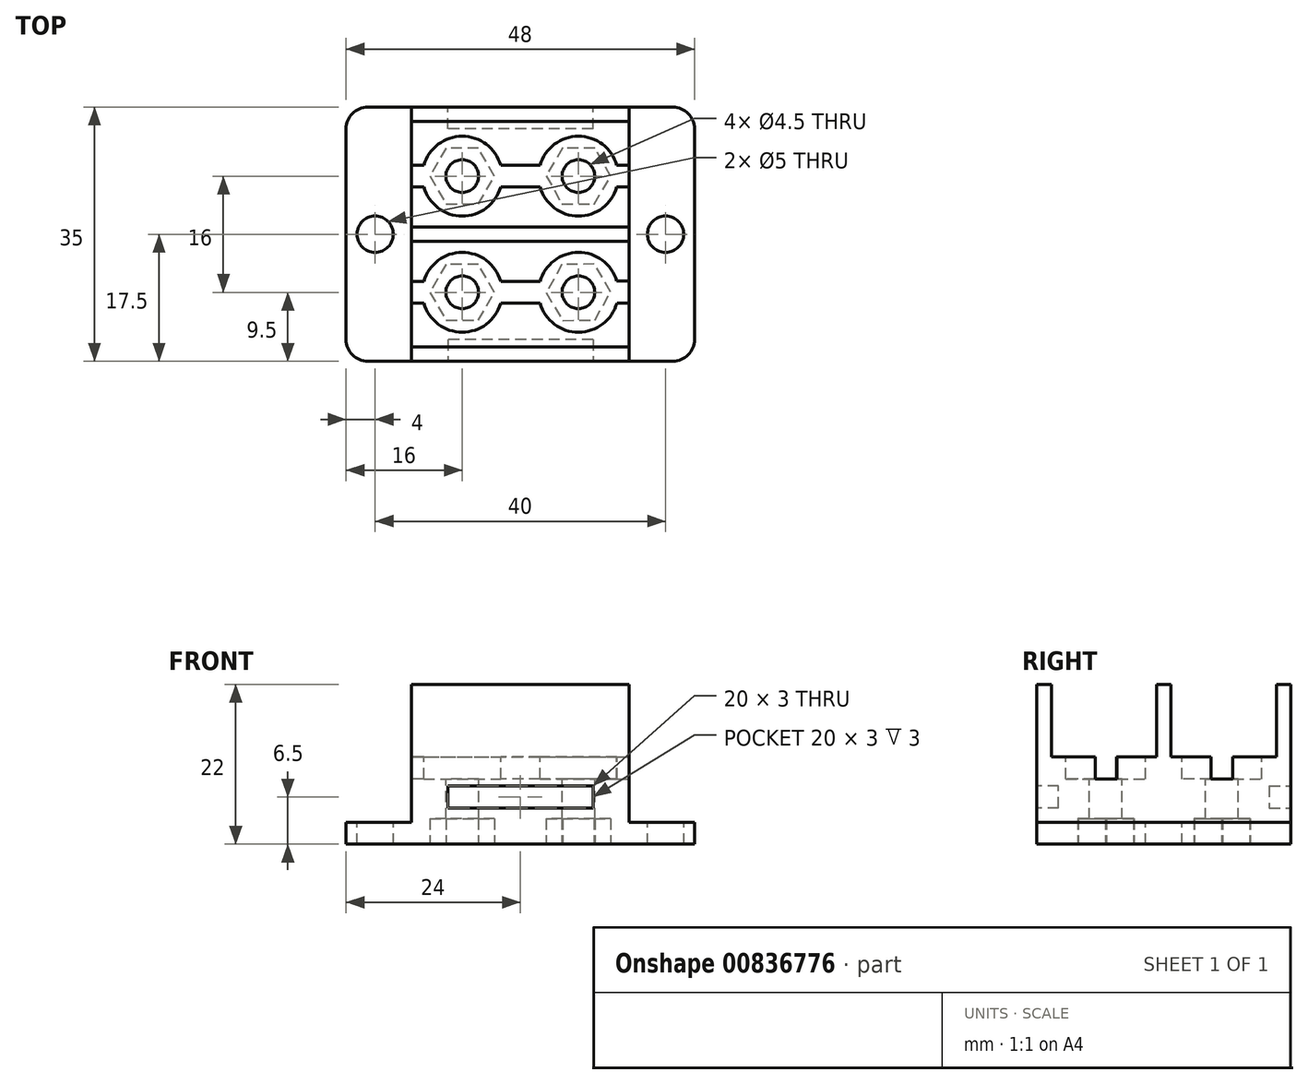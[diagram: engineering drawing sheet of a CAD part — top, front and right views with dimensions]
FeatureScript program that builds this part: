
annotation { "Feature Type Name" : "Feature", "Feature Type Description" : "" }
export const myFeature = defineFeature(function(context is Context, id is Id, definition is map)
    precondition{}
    {
        {
            var Q0;
            Q0=qCreatedBy(makeId("Front.planeOp"),FACE);
            var sketch = newSketch(context, id + "F0", { "sketchPlane" : qUnion([Q0])});
            skLineSegment(sketch, "E0", {"start": v(0, 0) * mm, "end": v(-9, 0) * mm});
            skLineSegment(sketch, "E1", {"start": v(-9, 0) * mm, "end": v(-9, 3) * mm});
            skLineSegment(sketch, "E2", {"start": v(-9, 3) * mm, "end": v(0, 3) * mm});
            skLineSegment(sketch, "E3", {"start": v(0, 3) * mm, "end": v(0, 12) * mm});
            skLineSegment(sketch, "E4", {"start": v(0, 12) * mm, "end": v(30, 12) * mm});
            skLineSegment(sketch, "E5", {"start": v(30, 12) * mm, "end": v(30, 3) * mm});
            skLineSegment(sketch, "E6", {"start": v(30, 3) * mm, "end": v(39, 3) * mm});
            skLineSegment(sketch, "E7", {"start": v(39, 3) * mm, "end": v(39, 0) * mm});
            skLineSegment(sketch, "E8", {"start": v(39, 0) * mm, "end": v(0, 0) * mm});
            skSolve(sketch);
        }
        {
            var Q0;
            Q0=makeQuery(id+"F0.imprint","IMPRINT",FACE,{"disambiguationData":[TD([[makeQuery(id+"F0.imprint","IMPRINT",EDGE,{"derivedFrom":sQuery(id+"F0.wireOp",EDGE,"E0")}),-1.0]])]});
            extrude(context, id + "F1", {"entities" : qUnion([Q0]), "oppositeDirection" : true, "depth" : 35 * mm, "offsetDistance" : 25 * mm});
        }
        {
            var Q0;
            Q0=qCreatedBy(makeId("Top.planeOp"),FACE);
            var Q1;
            Q1=makeQuery(id+"F1.opExtrude","CAP_VERTEX",VERTEX,{"disambiguationData":[OSD([sQuery(id+"F0.wireOp",EDGE,"E3"),sQuery(id+"F0.wireOp",EDGE,"E4")])],"isStart":false});
            cPlane(context, id + "F2", {"entities" : qUnion([Q0, Q1]), "cplaneType" : CPlaneType.PLANE_POINT, "offset" : 25 * mm, "width" : 150 * mm, "height" : 150 * mm});
        }
        {
            var Q0;
            Q0=qCreatedBy(id+"F2.planeOp",FACE);
            var sketch = newSketch(context, id + "F3", { "sketchPlane" : qUnion([Q0])});
            skLineSegment(sketch, "E9", {"start": v(23, 53.6) * mm, "end": v(23, -24.59) * mm, "construction": true});
            skLineSegment(sketch, "E10", {"start": v(7, 50.62) * mm, "end": v(7, -28.29) * mm, "construction": true});
            skLineSegment(sketch, "E11", {"start": v(23.6, 25.5) * mm, "end": v(1.01, 25.5) * mm, "construction": true});
            skLineSegment(sketch, "E12", {"start": v(28.02, 9.5) * mm, "end": v(4.88, 9.5) * mm, "construction": true});
            skCircle(sketch, "E13", {"center": v(23, 25.5) * mm, "radius": 2.25 * mm});
            skCircle(sketch, "E14", {"center": v(23, 9.5) * mm, "radius": 2.25 * mm});
            skCircle(sketch, "E15", {"center": v(7, 25.5) * mm, "radius": 2.25 * mm});
            skCircle(sketch, "E16", {"center": v(7, 9.5) * mm, "radius": 2.25 * mm});
            skLineSegment(sketch, "E17.bottom", {"start": v(29.45, 0) * mm, "end": v(0, 0) * mm});
            skLineSegment(sketch, "E18.bottom", {"start": v(8.68, 27) * mm, "end": v(21.32, 27) * mm});
            skLineSegment(sketch, "E18.top", {"start": v(8.68, 24) * mm, "end": v(21.32, 24) * mm});
            skLineSegment(sketch, "E18.left", {"start": v(8.68, 27) * mm, "end": v(8.68, 24) * mm});
            skLineSegment(sketch, "E18.right", {"start": v(21.32, 27) * mm, "end": v(21.32, 24) * mm});
            skLineSegment(sketch, "E19", {"start": v(8.68, 11) * mm, "end": v(21.32, 11) * mm});
            skLineSegment(sketch, "E20", {"start": v(21.32, 11) * mm, "end": v(21.32, 8) * mm});
            skLineSegment(sketch, "E21", {"start": v(21.32, 8) * mm, "end": v(8.68, 8) * mm});
            skLineSegment(sketch, "E22", {"start": v(8.68, 8) * mm, "end": v(8.68, 11) * mm});
            skCircle(sketch, "E23", {"center": v(7, 25.5) * mm, "radius": 5.5 * mm});
            skCircle(sketch, "E24", {"center": v(23, 25.5) * mm, "radius": 5.5 * mm});
            skCircle(sketch, "E25", {"center": v(7, 9.5) * mm, "radius": 5.5 * mm});
            skCircle(sketch, "E26", {"center": v(23, 9.5) * mm, "radius": 5.5 * mm});
            skLineSegment(sketch, "E27.bottom", {"start": v(28.3, 27) * mm, "end": v(30.07, 27) * mm});
            skLineSegment(sketch, "E28.bottom", {"start": v(5.32, 27) * mm, "end": v(0, 27) * mm});
            skLineSegment(sketch, "E28.top", {"start": v(5.32, 24) * mm, "end": v(0, 24) * mm});
            skLineSegment(sketch, "E28.left", {"start": v(5.32, 27) * mm, "end": v(5.32, 24) * mm});
            skLineSegment(sketch, "E28.right", {"start": v(0, 27) * mm, "end": v(0, 24) * mm});
            skLineSegment(sketch, "E29.bottom", {"start": v(24.68, 27) * mm, "end": v(30, 27) * mm});
            skLineSegment(sketch, "E29.top", {"start": v(24.68, 24) * mm, "end": v(30, 24) * mm});
            skLineSegment(sketch, "E29.left", {"start": v(24.68, 27) * mm, "end": v(24.68, 24) * mm});
            skLineSegment(sketch, "E29.right", {"start": v(30, 27) * mm, "end": v(30, 24) * mm});
            skLineSegment(sketch, "E30.bottom", {"start": v(5.32, 11) * mm, "end": v(0, 11) * mm});
            skLineSegment(sketch, "E30.top", {"start": v(5.32, 8) * mm, "end": v(0, 8) * mm});
            skLineSegment(sketch, "E30.left", {"start": v(5.32, 11) * mm, "end": v(5.32, 8) * mm});
            skLineSegment(sketch, "E30.right", {"start": v(0, 11) * mm, "end": v(0, 8) * mm});
            skLineSegment(sketch, "E31.bottom", {"start": v(24.64, 11.04) * mm, "end": v(30, 11.04) * mm});
            skLineSegment(sketch, "E31.top", {"start": v(24.64, 8.04) * mm, "end": v(30, 8.04) * mm});
            skLineSegment(sketch, "E31.left", {"start": v(24.64, 11.04) * mm, "end": v(24.64, 8.04) * mm});
            skLineSegment(sketch, "E31.right", {"start": v(30, 11.04) * mm, "end": v(30, 8.04) * mm});
            skSolve(sketch);
        }
        {
            var Q0;
            Q0=makeQuery(id+"F1.opExtrude","SWEPT_FACE",FACE,{"disambiguationData":[OSD([sQuery(id+"F0.wireOp",EDGE,"E6")])]});
            var sketch = newSketch(context, id + "F4", { "sketchPlane" : qUnion([Q0])});
            skCircle(sketch, "E32", {"center": v(-5, 17.5) * mm, "radius": 2.5 * mm});
            skCircle(sketch, "E33", {"center": v(35, 17.5) * mm, "radius": 2.5 * mm});
            skSolve(sketch);
        }
        {
            var Q0;
            Q0=makeQuery(id+"F4.imprint","IMPRINT",FACE,{"disambiguationData":[TD([[makeQuery(id+"F4.imprint","IMPRINT",EDGE,{"derivedFrom":sQuery(id+"F4.wireOp",EDGE,"E32")}),1.0]])]});
            var Q1;
            Q1=makeQuery(id+"F4.imprint","IMPRINT",FACE,{"disambiguationData":[TD([[makeQuery(id+"F4.imprint","IMPRINT",EDGE,{"derivedFrom":sQuery(id+"F4.wireOp",EDGE,"E33")}),1.0]])]});
            extrude(context, id + "F5", {"entities" : qUnion([Q0, Q1]), "operationType" : NewBodyOperationType.REMOVE, "endBound" : BoundingType.UP_TO_NEXT, "oppositeDirection" : true, "depth" : 25 * mm, "offsetDistance" : 25 * mm});
        }
        {
            var Q0;
            Q0=makeQuery(id+"F1.opExtrude","CAP_EDGE",EDGE,{"disambiguationData":[OSD([sQuery(id+"F0.wireOp",EDGE,"E1")])],"isStart":false});
            var Q1;
            Q1=makeQuery(id+"F1.opExtrude","CAP_EDGE",EDGE,{"disambiguationData":[OSD([sQuery(id+"F0.wireOp",EDGE,"E7")])],"isStart":false});
            var Q2;
            Q2=makeQuery(id+"F1.opExtrude","CAP_EDGE",EDGE,{"disambiguationData":[OSD([sQuery(id+"F0.wireOp",EDGE,"E7")])],"isStart":true});
            var Q3;
            Q3=makeQuery(id+"F1.opExtrude","CAP_EDGE",EDGE,{"disambiguationData":[OSD([sQuery(id+"F0.wireOp",EDGE,"E1")])],"isStart":true});
            fillet(context, id + "F6", {"entities" : qUnion([Q0, Q1, Q2, Q3]), "radius" : 3 * mm, "tangentPropagation" : true, "allowEdgeOverflow" : false});
        }
        {
            var Q0;
            Q0=makeQuery(id+"F1.opExtrude","SWEPT_FACE",FACE,{"disambiguationData":[OSD([sQuery(id+"F0.wireOp",EDGE,"E4")])]});
            var sketch = newSketch(context, id + "F7", { "sketchPlane" : qUnion([Q0])});
            skLineSegment(sketch, "E34.bottom", {"start": v(0, 35) * mm, "end": v(30, 35) * mm});
            skLineSegment(sketch, "E34.top", {"start": v(0, 33) * mm, "end": v(30, 33) * mm});
            skLineSegment(sketch, "E34.left", {"start": v(0, 35) * mm, "end": v(0, 33) * mm});
            skLineSegment(sketch, "E34.right", {"start": v(30, 35) * mm, "end": v(30, 33) * mm});
            skLineSegment(sketch, "E35.bottom", {"start": v(0, 18.5) * mm, "end": v(30, 18.5) * mm});
            skLineSegment(sketch, "E35.top", {"start": v(0, 16.5) * mm, "end": v(30, 16.5) * mm});
            skLineSegment(sketch, "E35.left", {"start": v(0, 18.5) * mm, "end": v(0, 16.5) * mm});
            skLineSegment(sketch, "E35.right", {"start": v(30, 18.5) * mm, "end": v(30, 16.5) * mm});
            skLineSegment(sketch, "E36.bottom", {"start": v(0, 0) * mm, "end": v(30, 0) * mm});
            skLineSegment(sketch, "E36.top", {"start": v(0, 2) * mm, "end": v(30, 2) * mm});
            skLineSegment(sketch, "E36.left", {"start": v(0, 0) * mm, "end": v(0, 2) * mm});
            skLineSegment(sketch, "E36.right", {"start": v(30, 0) * mm, "end": v(30, 2) * mm});
            skSolve(sketch);
        }
        {
            var Q0;
            Q0=makeQuery(id+"F7.imprint","IMPRINT",FACE,{"disambiguationData":[TD([[makeQuery(id+"F7.imprint","IMPRINT",EDGE,{"derivedFrom":sQuery(id+"F7.wireOp",EDGE,"E34.bottom")}),-1.0]])]});
            var Q1;
            Q1=makeQuery(id+"F7.imprint","IMPRINT",FACE,{"disambiguationData":[TD([[makeQuery(id+"F7.imprint","IMPRINT",EDGE,{"derivedFrom":sQuery(id+"F7.wireOp",EDGE,"E35.bottom")}),-1.0]])]});
            var Q2;
            Q2=makeQuery(id+"F7.imprint","IMPRINT",FACE,{"disambiguationData":[TD([[makeQuery(id+"F7.imprint","IMPRINT",EDGE,{"derivedFrom":sQuery(id+"F7.wireOp",EDGE,"E36.bottom")}),1.0]])]});
            extrude(context, id + "F8", {"entities" : qUnion([Q0, Q1, Q2]), "operationType" : NewBodyOperationType.ADD, "depth" : 10 * mm, "offsetDistance" : 25 * mm});
        }
        {
            var Q0;
            {var subQ0=sQuery(id+"F3.wireOp",EDGE,"E18.left");Q0=makeQuery(id+"F3.imprint","IMPRINT",FACE,{"disambiguationData":[TD([[makeQuery(id+"F3.imprint","IMPRINT",EDGE,{"derivedFrom":subQ0}),-1.0]])]});}
            var Q1;
            {var subQ0=sQuery(id+"F3.wireOp",EDGE,"E28.left");Q1=makeQuery(id+"F3.imprint","IMPRINT",FACE,{"disambiguationData":[TD([[makeQuery(id+"F3.imprint","IMPRINT",EDGE,{"derivedFrom":subQ0}),-1.0]])]});}
            var Q2;
            {var subQ0=sQuery(id+"F3.wireOp",EDGE,"E18.left");Q2=makeQuery(id+"F3.imprint","IMPRINT",FACE,{"disambiguationData":[TD([[makeQuery(id+"F3.imprint","IMPRINT",EDGE,{"derivedFrom":subQ0}),1.0]])]});}
            var Q3;
            {var subQ0=sQuery(id+"F3.wireOp",EDGE,"E18.right");Q3=makeQuery(id+"F3.imprint","IMPRINT",FACE,{"disambiguationData":[TD([[makeQuery(id+"F3.imprint","IMPRINT",EDGE,{"derivedFrom":subQ0}),-1.0]])]});}
            var Q4;
            {var subQ0=sQuery(id+"F3.wireOp",EDGE,"E29.left");Q4=makeQuery(id+"F3.imprint","IMPRINT",FACE,{"disambiguationData":[TD([[makeQuery(id+"F3.imprint","IMPRINT",EDGE,{"derivedFrom":subQ0}),1.0]])]});}
            var Q5;
            {var subQ0=sQuery(id+"F3.wireOp",EDGE,"E18.right");Q5=makeQuery(id+"F3.imprint","IMPRINT",FACE,{"disambiguationData":[TD([[makeQuery(id+"F3.imprint","IMPRINT",EDGE,{"derivedFrom":subQ0}),1.0]])]});}
            var Q6;
            {var subQ0=sQuery(id+"F3.wireOp",EDGE,"E22");Q6=makeQuery(id+"F3.imprint","IMPRINT",FACE,{"disambiguationData":[TD([[makeQuery(id+"F3.imprint","IMPRINT",EDGE,{"derivedFrom":subQ0}),1.0]])]});}
            var Q7;
            {var subQ0=sQuery(id+"F3.wireOp",EDGE,"E22");Q7=makeQuery(id+"F3.imprint","IMPRINT",FACE,{"disambiguationData":[TD([[makeQuery(id+"F3.imprint","IMPRINT",EDGE,{"derivedFrom":subQ0}),-1.0]])]});}
            var Q8;
            {var subQ0=sQuery(id+"F3.wireOp",EDGE,"E30.left");Q8=makeQuery(id+"F3.imprint","IMPRINT",FACE,{"disambiguationData":[TD([[makeQuery(id+"F3.imprint","IMPRINT",EDGE,{"derivedFrom":subQ0}),-1.0]])]});}
            var Q9;
            {var subQ0=sQuery(id+"F3.wireOp",EDGE,"E20");Q9=makeQuery(id+"F3.imprint","IMPRINT",FACE,{"disambiguationData":[TD([[makeQuery(id+"F3.imprint","IMPRINT",EDGE,{"derivedFrom":subQ0}),-1.0]])]});}
            var Q10;
            {var subQ0=sQuery(id+"F3.wireOp",EDGE,"E31.left");Q10=makeQuery(id+"F3.imprint","IMPRINT",FACE,{"disambiguationData":[TD([[makeQuery(id+"F3.imprint","IMPRINT",EDGE,{"derivedFrom":subQ0}),1.0]])]});}
            var Q11;
            {var subQ4=sQuery(id+"F3.wireOp",EDGE,"E20");Q11=makeQuery(id+"F3.imprint","IMPRINT",FACE,{"disambiguationData":[TD([[makeQuery(id+"F3.imprint","IMPRINT",EDGE,{"derivedFrom":subQ4}),1.0]])]});}
            extrude(context, id + "F9", {"entities" : qUnion([Q0, Q1, Q2, Q3, Q4, Q5, Q6, Q7, Q8, Q9, Q10, Q11]), "operationType" : NewBodyOperationType.REMOVE, "endBound" : BoundingType.UP_TO_NEXT, "oppositeDirection" : true, "depth" : 25 * mm, "offsetDistance" : 25 * mm});
        }
        {
            var Q0;
            {var subQ0=sQuery(id+"F3.wireOp",EDGE,"E21");var subQ5=sQuery(id+"F3.wireOp",EDGE,"E25");var subQ6=makeQuery(id+"F3.imprint","INTERSECT",VERTEX,{"derivedFrom":[subQ0,subQ5]});Q0=makeQuery(id+"F3.imprint","IMPRINT",FACE,{"disambiguationData":[TD([[makeQuery(id+"F3.imprint","IMPRINT",EDGE,{"disambiguationData":[TD([[subQ6,1.0]])],"derivedFrom":subQ5}),1.0]])]});}
            var Q1;
            {var subQ1=sQuery(id+"F3.wireOp",EDGE,"E30.bottom");var subQ6=sQuery(id+"F3.wireOp",EDGE,"E25");var subQ7=makeQuery(id+"F3.imprint","INTERSECT",VERTEX,{"derivedFrom":[subQ6,subQ1]});Q1=makeQuery(id+"F3.imprint","IMPRINT",FACE,{"disambiguationData":[TD([[makeQuery(id+"F3.imprint","IMPRINT",EDGE,{"disambiguationData":[TD([[subQ7,-1.0]])],"derivedFrom":subQ6}),1.0]])]});}
            var Q2;
            {var subQ0=sQuery(id+"F3.wireOp",EDGE,"E19");var subQ5=sQuery(id+"F3.wireOp",EDGE,"E25");var subQ6=makeQuery(id+"F3.imprint","INTERSECT",VERTEX,{"derivedFrom":[subQ0,subQ5]});Q2=makeQuery(id+"F3.imprint","IMPRINT",FACE,{"disambiguationData":[TD([[makeQuery(id+"F3.imprint","IMPRINT",EDGE,{"disambiguationData":[TD([[subQ6,-1.0]])],"derivedFrom":subQ5}),1.0]])]});}
            var Q3;
            {var subQ1=sQuery(id+"F3.wireOp",EDGE,"E19");var subQ6=sQuery(id+"F3.wireOp",EDGE,"E25");var subQ8=makeQuery(id+"F3.imprint","INTERSECT",VERTEX,{"derivedFrom":[subQ1,subQ6]});Q3=makeQuery(id+"F3.imprint","IMPRINT",FACE,{"disambiguationData":[TD([[makeQuery(id+"F3.imprint","IMPRINT",EDGE,{"disambiguationData":[TD([[subQ8,1.0]])],"derivedFrom":subQ6}),1.0]])]});}
            var Q4;
            {var subQ0=sQuery(id+"F3.wireOp",EDGE,"E19");var subQ5=sQuery(id+"F3.wireOp",EDGE,"E26");var subQ6=makeQuery(id+"F3.imprint","INTERSECT",VERTEX,{"derivedFrom":[subQ0,subQ5]});Q4=makeQuery(id+"F3.imprint","IMPRINT",FACE,{"disambiguationData":[TD([[makeQuery(id+"F3.imprint","IMPRINT",EDGE,{"disambiguationData":[TD([[subQ6,1.0]])],"derivedFrom":subQ5}),1.0]])]});}
            var Q5;
            {var subQ1=sQuery(id+"F3.wireOp",EDGE,"E19");var subQ6=sQuery(id+"F3.wireOp",EDGE,"E26");var subQ7=makeQuery(id+"F3.imprint","INTERSECT",VERTEX,{"derivedFrom":[subQ1,subQ6]});Q5=makeQuery(id+"F3.imprint","IMPRINT",FACE,{"disambiguationData":[TD([[makeQuery(id+"F3.imprint","IMPRINT",EDGE,{"disambiguationData":[TD([[subQ7,-1.0]])],"derivedFrom":subQ6}),1.0]])]});}
            var Q6;
            {var subQ0=sQuery(id+"F3.wireOp",EDGE,"E21");var subQ5=sQuery(id+"F3.wireOp",EDGE,"E26");var subQ6=makeQuery(id+"F3.imprint","INTERSECT",VERTEX,{"derivedFrom":[subQ0,subQ5]});Q6=makeQuery(id+"F3.imprint","IMPRINT",FACE,{"disambiguationData":[TD([[makeQuery(id+"F3.imprint","IMPRINT",EDGE,{"disambiguationData":[TD([[subQ6,-1.0]])],"derivedFrom":subQ5}),1.0]])]});}
            var Q7;
            {var subQ0=sQuery(id+"F3.wireOp",EDGE,"E31.bottom");var subQ5=sQuery(id+"F3.wireOp",EDGE,"E26");var subQ6=makeQuery(id+"F3.imprint","INTERSECT",VERTEX,{"derivedFrom":[subQ5,subQ0]});Q7=makeQuery(id+"F3.imprint","IMPRINT",FACE,{"disambiguationData":[TD([[makeQuery(id+"F3.imprint","IMPRINT",EDGE,{"disambiguationData":[TD([[subQ6,1.0]])],"derivedFrom":subQ5}),1.0]])]});}
            var Q8;
            {var subQ0=sQuery(id+"F3.wireOp",EDGE,"E18.top");var subQ5=sQuery(id+"F3.wireOp",EDGE,"E24");var subQ6=makeQuery(id+"F3.imprint","INTERSECT",VERTEX,{"derivedFrom":[subQ0,subQ5]});Q8=makeQuery(id+"F3.imprint","IMPRINT",FACE,{"disambiguationData":[TD([[makeQuery(id+"F3.imprint","IMPRINT",EDGE,{"disambiguationData":[TD([[subQ6,-1.0]])],"derivedFrom":subQ5}),1.0]])]});}
            var Q9;
            {var subQ1=sQuery(id+"F3.wireOp",EDGE,"E29.bottom");var subQ6=sQuery(id+"F3.wireOp",EDGE,"E24");var subQ7=makeQuery(id+"F3.imprint","INTERSECT",VERTEX,{"derivedFrom":[subQ6,subQ1]});Q9=makeQuery(id+"F3.imprint","IMPRINT",FACE,{"disambiguationData":[TD([[makeQuery(id+"F3.imprint","IMPRINT",EDGE,{"disambiguationData":[TD([[subQ7,1.0]])],"derivedFrom":subQ6}),1.0]])]});}
            var Q10;
            {var subQ0=sQuery(id+"F3.wireOp",EDGE,"E18.bottom");var subQ5=sQuery(id+"F3.wireOp",EDGE,"E24");var subQ6=makeQuery(id+"F3.imprint","INTERSECT",VERTEX,{"derivedFrom":[subQ0,subQ5]});Q10=makeQuery(id+"F3.imprint","IMPRINT",FACE,{"disambiguationData":[TD([[makeQuery(id+"F3.imprint","IMPRINT",EDGE,{"disambiguationData":[TD([[subQ6,1.0]])],"derivedFrom":subQ5}),1.0]])]});}
            var Q11;
            {var subQ1=sQuery(id+"F3.wireOp",EDGE,"E18.bottom");var subQ6=sQuery(id+"F3.wireOp",EDGE,"E24");var subQ8=makeQuery(id+"F3.imprint","INTERSECT",VERTEX,{"derivedFrom":[subQ1,subQ6]});Q11=makeQuery(id+"F3.imprint","IMPRINT",FACE,{"disambiguationData":[TD([[makeQuery(id+"F3.imprint","IMPRINT",EDGE,{"disambiguationData":[TD([[subQ8,-1.0]])],"derivedFrom":subQ6}),1.0]])]});}
            var Q12;
            {var subQ0=sQuery(id+"F3.wireOp",EDGE,"E18.top");var subQ5=sQuery(id+"F3.wireOp",EDGE,"E23");var subQ7=makeQuery(id+"F3.imprint","INTERSECT",VERTEX,{"derivedFrom":[subQ0,subQ5]});Q12=makeQuery(id+"F3.imprint","IMPRINT",FACE,{"disambiguationData":[TD([[makeQuery(id+"F3.imprint","IMPRINT",EDGE,{"disambiguationData":[TD([[subQ7,1.0]])],"derivedFrom":subQ5}),1.0]])]});}
            var Q13;
            {var subQ0=sQuery(id+"F3.wireOp",EDGE,"E18.bottom");var subQ5=sQuery(id+"F3.wireOp",EDGE,"E23");var subQ7=makeQuery(id+"F3.imprint","INTERSECT",VERTEX,{"derivedFrom":[subQ0,subQ5]});Q13=makeQuery(id+"F3.imprint","IMPRINT",FACE,{"disambiguationData":[TD([[makeQuery(id+"F3.imprint","IMPRINT",EDGE,{"disambiguationData":[TD([[subQ7,-1.0]])],"derivedFrom":subQ5}),1.0]])]});}
            var Q14;
            {var subQ1=sQuery(id+"F3.wireOp",EDGE,"E18.bottom");var subQ6=sQuery(id+"F3.wireOp",EDGE,"E23");var subQ7=makeQuery(id+"F3.imprint","INTERSECT",VERTEX,{"derivedFrom":[subQ1,subQ6]});Q14=makeQuery(id+"F3.imprint","IMPRINT",FACE,{"disambiguationData":[TD([[makeQuery(id+"F3.imprint","IMPRINT",EDGE,{"disambiguationData":[TD([[subQ7,1.0]])],"derivedFrom":subQ6}),1.0]])]});}
            var Q15;
            {var subQ1=sQuery(id+"F3.wireOp",EDGE,"E28.bottom");var subQ6=sQuery(id+"F3.wireOp",EDGE,"E23");var subQ7=makeQuery(id+"F3.imprint","INTERSECT",VERTEX,{"derivedFrom":[subQ6,subQ1]});Q15=makeQuery(id+"F3.imprint","IMPRINT",FACE,{"disambiguationData":[TD([[makeQuery(id+"F3.imprint","IMPRINT",EDGE,{"disambiguationData":[TD([[subQ7,-1.0]])],"derivedFrom":subQ6}),1.0]])]});}
            extrude(context, id + "F10", {"entities" : qUnion([Q0, Q1, Q2, Q3, Q4, Q5, Q6, Q7, Q8, Q9, Q10, Q11, Q12, Q13, Q14, Q15]), "operationType" : NewBodyOperationType.REMOVE, "oppositeDirection" : true, "depth" : 3 * mm, "offsetDistance" : 25 * mm});
        }
        {
            var Q0;
            Q0 = qSketchRegion(id + "F3", true);
            extrude(context, id + "F11", {"entities" : qUnion([Q0]), "operationType" : NewBodyOperationType.REMOVE, "oppositeDirection" : true, "depth" : 3 * mm, "offsetDistance" : 25 * mm});
        }
        {
            var Q0;
            Q0=makeQuery(id+"F8.boolean.opBoolean","MERGE",FACE,{"derivedFrom":[makeQuery(id+"F1.opExtrude","CAP_FACE",FACE,{"disambiguationData":[OSD([sQuery(id+"F0.wireOp",EDGE,"E0"),sQuery(id+"F0.wireOp",EDGE,"E1"),sQuery(id+"F0.wireOp",EDGE,"E2"),sQuery(id+"F0.wireOp",EDGE,"E3"),sQuery(id+"F0.wireOp",EDGE,"E4"),sQuery(id+"F0.wireOp",EDGE,"E5"),sQuery(id+"F0.wireOp",EDGE,"E6"),sQuery(id+"F0.wireOp",EDGE,"E7"),sQuery(id+"F0.wireOp",EDGE,"E8")])],"isStart":true}),makeQuery(id+"F8.opExtrude","SWEPT_FACE",FACE,{"disambiguationData":[OSD([sQuery(id+"F7.wireOp",EDGE,"E36.bottom")])]})]});
            var sketch = newSketch(context, id + "F12", { "sketchPlane" : qUnion([Q0])});
            skLineSegment(sketch, "E37.bottom", {"start": v(25, 5) * mm, "end": v(5, 5) * mm});
            skLineSegment(sketch, "E37.top", {"start": v(25, 8) * mm, "end": v(5, 8) * mm});
            skLineSegment(sketch, "E37.left", {"start": v(25, 5) * mm, "end": v(25, 8) * mm});
            skLineSegment(sketch, "E37.right", {"start": v(5, 5) * mm, "end": v(5, 8) * mm});
            skSolve(sketch);
        }
        {
            var Q0;
            Q0=makeQuery(id+"F12.imprint","IMPRINT",FACE,{"disambiguationData":[TD([[makeQuery(id+"F12.imprint","IMPRINT",EDGE,{"derivedFrom":sQuery(id+"F12.wireOp",EDGE,"E37.bottom")}),-1.0]])]});
            extrude(context, id + "F13", {"entities" : qUnion([Q0]), "operationType" : NewBodyOperationType.REMOVE, "oppositeDirection" : true, "depth" : 3 * mm, "offsetDistance" : 25 * mm});
        }
        {
            var Q0;
            Q0=makeQuery(id+"F8.boolean.opBoolean","MERGE",FACE,{"derivedFrom":[makeQuery(id+"F1.opExtrude","CAP_FACE",FACE,{"disambiguationData":[OSD([sQuery(id+"F0.wireOp",EDGE,"E0"),sQuery(id+"F0.wireOp",EDGE,"E1"),sQuery(id+"F0.wireOp",EDGE,"E2"),sQuery(id+"F0.wireOp",EDGE,"E3"),sQuery(id+"F0.wireOp",EDGE,"E4"),sQuery(id+"F0.wireOp",EDGE,"E5"),sQuery(id+"F0.wireOp",EDGE,"E6"),sQuery(id+"F0.wireOp",EDGE,"E7"),sQuery(id+"F0.wireOp",EDGE,"E8")])],"isStart":false}),makeQuery(id+"F8.opExtrude","SWEPT_FACE",FACE,{"disambiguationData":[OSD([sQuery(id+"F7.wireOp",EDGE,"E34.bottom")])]})]});
            var sketch = newSketch(context, id + "F14", { "sketchPlane" : qUnion([Q0])});
            skLineSegment(sketch, "E38.bottom", {"start": v(-25, 8) * mm, "end": v(-5, 8) * mm});
            skLineSegment(sketch, "E38.top", {"start": v(-25, 5) * mm, "end": v(-5, 5) * mm});
            skLineSegment(sketch, "E38.left", {"start": v(-25, 8) * mm, "end": v(-25, 5) * mm});
            skLineSegment(sketch, "E38.right", {"start": v(-5, 8) * mm, "end": v(-5, 5) * mm});
            skSolve(sketch);
        }
        {
            var Q0;
            Q0=makeQuery(id+"F14.imprint","IMPRINT",FACE,{"disambiguationData":[TD([[makeQuery(id+"F14.imprint","IMPRINT",EDGE,{"derivedFrom":sQuery(id+"F14.wireOp",EDGE,"E38.bottom")}),-1.0]])]});
            extrude(context, id + "F15", {"entities" : qUnion([Q0]), "operationType" : NewBodyOperationType.REMOVE, "oppositeDirection" : true, "depth" : 3 * mm, "offsetDistance" : 25 * mm});
        }
        {
            var Q0;
            Q0=makeQuery(id+"F1.opExtrude","SWEPT_FACE",FACE,{"disambiguationData":[OSD([sQuery(id+"F0.wireOp",EDGE,"E0"),sQuery(id+"F0.wireOp",EDGE,"E8")])]});
            var sketch = newSketch(context, id + "F16", { "sketchPlane" : qUnion([Q0])});
            skCircle(sketch, "E39.cCircle", {"center": v(23, -25.5) * mm, "radius": 3.85 * mm, "construction": true});
            skLineSegment(sketch, "E39.0", {"start": v(18.55, -25.56) * mm, "end": v(20.73, -21.68) * mm});
            skLineSegment(sketch, "E39.1", {"start": v(20.73, -21.68) * mm, "end": v(25.17, -21.62) * mm});
            skLineSegment(sketch, "E39.2", {"start": v(25.17, -21.62) * mm, "end": v(27.45, -25.44) * mm});
            skLineSegment(sketch, "E39.3", {"start": v(27.45, -25.44) * mm, "end": v(25.27, -29.32) * mm});
            skLineSegment(sketch, "E39.4", {"start": v(25.27, -29.32) * mm, "end": v(20.83, -29.38) * mm});
            skLineSegment(sketch, "E39.5", {"start": v(20.83, -29.38) * mm, "end": v(18.55, -25.56) * mm});
            skPoint(sketch, "E39.0.midPoint", {"position": v(19.64, -23.62) * mm});
            skCircle(sketch, "E40.cCircle", {"center": v(7, -25.5) * mm, "radius": 3.85 * mm, "construction": true});
            skLineSegment(sketch, "E40.0", {"start": v(11.45, -25.49) * mm, "end": v(9.24, -29.34) * mm});
            skLineSegment(sketch, "E40.1", {"start": v(9.24, -29.34) * mm, "end": v(4.79, -29.36) * mm});
            skLineSegment(sketch, "E40.2", {"start": v(4.79, -29.36) * mm, "end": v(2.55, -25.51) * mm});
            skLineSegment(sketch, "E40.3", {"start": v(2.55, -25.51) * mm, "end": v(4.76, -21.66) * mm});
            skLineSegment(sketch, "E40.4", {"start": v(4.76, -21.66) * mm, "end": v(9.21, -21.64) * mm});
            skLineSegment(sketch, "E40.5", {"start": v(9.21, -21.64) * mm, "end": v(11.45, -25.49) * mm});
            skPoint(sketch, "E40.0.midPoint", {"position": v(10.34, -27.41) * mm});
            skCircle(sketch, "E41.cCircle", {"center": v(23, -9.5) * mm, "radius": 3.85 * mm, "construction": true});
            skLineSegment(sketch, "E41.0", {"start": v(20.73, -13.32) * mm, "end": v(18.55, -9.44) * mm});
            skLineSegment(sketch, "E41.1", {"start": v(18.55, -9.44) * mm, "end": v(20.83, -5.62) * mm});
            skLineSegment(sketch, "E41.2", {"start": v(20.83, -5.62) * mm, "end": v(25.27, -5.68) * mm});
            skLineSegment(sketch, "E41.3", {"start": v(25.27, -5.68) * mm, "end": v(27.45, -9.56) * mm});
            skLineSegment(sketch, "E41.4", {"start": v(27.45, -9.56) * mm, "end": v(25.17, -13.38) * mm});
            skLineSegment(sketch, "E41.5", {"start": v(25.17, -13.38) * mm, "end": v(20.73, -13.32) * mm});
            skPoint(sketch, "E41.0.midPoint", {"position": v(19.64, -11.38) * mm});
            skCircle(sketch, "E42.cCircle", {"center": v(7, -9.5) * mm, "radius": 3.85 * mm, "construction": true});
            skLineSegment(sketch, "E42.0", {"start": v(9.22, -13.35) * mm, "end": v(4.78, -13.35) * mm});
            skLineSegment(sketch, "E42.1", {"start": v(4.78, -13.35) * mm, "end": v(2.55, -9.5) * mm});
            skLineSegment(sketch, "E42.2", {"start": v(2.55, -9.5) * mm, "end": v(4.78, -5.65) * mm});
            skLineSegment(sketch, "E42.3", {"start": v(4.78, -5.65) * mm, "end": v(9.22, -5.65) * mm});
            skLineSegment(sketch, "E42.4", {"start": v(9.22, -5.65) * mm, "end": v(11.45, -9.5) * mm});
            skLineSegment(sketch, "E42.5", {"start": v(11.45, -9.5) * mm, "end": v(9.22, -13.35) * mm});
            skPoint(sketch, "E42.0.midPoint", {"position": v(7, -13.35) * mm});
            skSolve(sketch);
        }
        {
            var Q0;
            Q0=makeQuery(id+"F16.imprint","IMPRINT",FACE,{"disambiguationData":[TD([[makeQuery(id+"F16.imprint","IMPRINT",EDGE,{"derivedFrom":sQuery(id+"F16.wireOp",EDGE,"E39.0")}),-1.0]])]});
            var Q1;
            Q1=makeQuery(id+"F16.imprint","IMPRINT",FACE,{"disambiguationData":[TD([[makeQuery(id+"F16.imprint","IMPRINT",EDGE,{"derivedFrom":sQuery(id+"F16.wireOp",EDGE,"E40.0")}),-1.0]])]});
            var Q2;
            Q2=makeQuery(id+"F16.imprint","IMPRINT",FACE,{"disambiguationData":[TD([[makeQuery(id+"F16.imprint","IMPRINT",EDGE,{"derivedFrom":sQuery(id+"F16.wireOp",EDGE,"E41.0")}),-1.0]])]});
            var Q3;
            Q3=makeQuery(id+"F16.imprint","IMPRINT",FACE,{"disambiguationData":[TD([[makeQuery(id+"F16.imprint","IMPRINT",EDGE,{"derivedFrom":sQuery(id+"F16.wireOp",EDGE,"E42.0")}),-1.0]])]});
            extrude(context, id + "F17", {"entities" : qUnion([Q0, Q1, Q2, Q3]), "operationType" : NewBodyOperationType.REMOVE, "oppositeDirection" : true, "depth" : 3.5 * mm, "offsetDistance" : 25 * mm});
        }
    });
